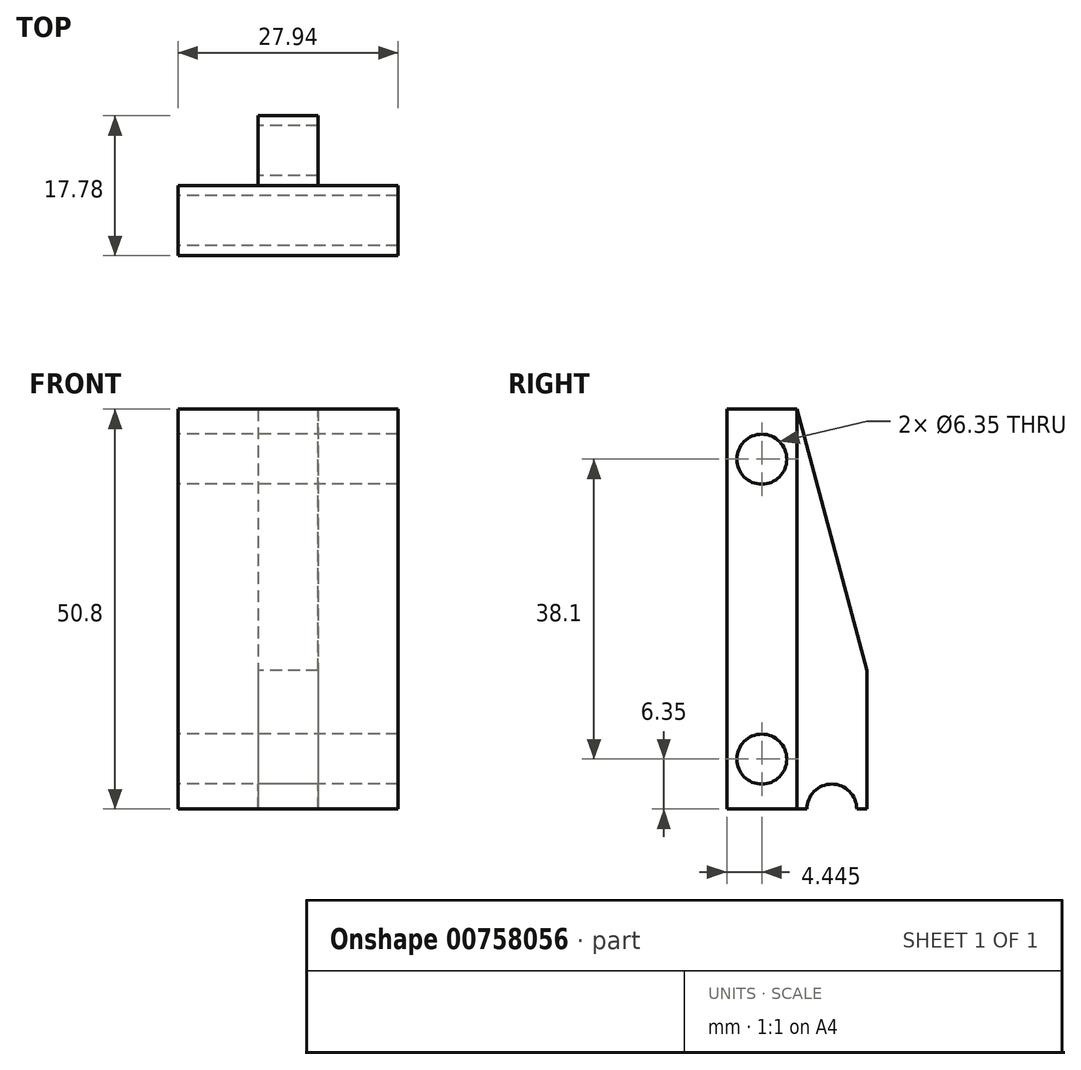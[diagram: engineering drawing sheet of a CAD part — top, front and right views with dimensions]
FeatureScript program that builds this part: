
annotation { "Feature Type Name" : "Feature", "Feature Type Description" : "" }
export const myFeature = defineFeature(function(context is Context, id is Id, definition is map)
    precondition{}
    {
        {
            var Q0;
            Q0=qCreatedBy(makeId("Top.planeOp"),FACE);
            var sketch = newSketch(context, id + "F0", { "sketchPlane" : qUnion([Q0])});
            skLineSegment(sketch, "E0.bottom", {"start": v(0, 0) * mm, "end": v(27.94, 0) * mm});
            skLineSegment(sketch, "E0.top", {"start": v(0, 17.78) * mm, "end": v(27.94, 17.78) * mm});
            skLineSegment(sketch, "E0.left", {"start": v(0, 0) * mm, "end": v(0, 17.78) * mm});
            skLineSegment(sketch, "E0.right", {"start": v(27.94, 0) * mm, "end": v(27.94, 17.78) * mm});
            skLineSegment(sketch, "E1.bottom", {"start": v(0, 8.89) * mm, "end": v(10.16, 8.89) * mm});
            skLineSegment(sketch, "E1.top", {"start": v(0, 17.78) * mm, "end": v(10.16, 17.78) * mm});
            skLineSegment(sketch, "E1.left", {"start": v(0, 8.89) * mm, "end": v(0, 17.78) * mm});
            skLineSegment(sketch, "E1.right", {"start": v(10.16, 8.89) * mm, "end": v(10.16, 17.78) * mm});
            skLineSegment(sketch, "E2.bottom", {"start": v(17.78, 17.78) * mm, "end": v(27.94, 17.78) * mm});
            skLineSegment(sketch, "E2.top", {"start": v(17.78, 8.89) * mm, "end": v(27.94, 8.89) * mm});
            skLineSegment(sketch, "E2.left", {"start": v(17.78, 17.78) * mm, "end": v(17.78, 8.89) * mm});
            skLineSegment(sketch, "E2.right", {"start": v(27.94, 17.78) * mm, "end": v(27.94, 8.89) * mm});
            skSolve(sketch);
        }
        {
            var Q0;
            {var subQ1=sQuery(id+"F0.wireOp",EDGE,"E0.bottom");Q0=makeQuery(id+"F0.imprint","IMPRINT",FACE,{"disambiguationData":[TD([[makeQuery(id+"F0.imprint","IMPRINT",EDGE,{"derivedFrom":subQ1}),1.0]])]});}
            extrude(context, id + "F1", {"entities" : qUnion([Q0]), "depth" : 50.8 * mm, "offsetDistance" : 25.4 * mm});
        }
        {
            var Q0;
            Q0=makeQuery(id+"F1.opExtrude","SWEPT_FACE",FACE,{"disambiguationData":[OSD([sQuery(id+"F0.wireOp",EDGE,"E1.right")])]});
            var sketch = newSketch(context, id + "F2", { "sketchPlane" : qUnion([Q0])});
            skLineSegment(sketch, "E3", {"start": v(-8.89, 50.8) * mm, "end": v(-17.78, 17.62) * mm});
            skCircle(sketch, "E4", {"center": v(-13.33, 0) * mm, "radius": 3.18 * mm});
            skSolve(sketch);
        }
        {
            var Q0;
            {var subQ0=sQuery(id+"F2.wireOp",EDGE,"E3");Q0=makeQuery(id+"F2.imprint","IMPRINT",FACE,{"disambiguationData":[TD([[makeQuery(id+"F2.imprint","IMPRINT",EDGE,{"derivedFrom":subQ0}),-1.0]])]});}
            var Q1;
            {var subQ0=sQuery(id+"F2.wireOp",EDGE,"E4");var subQ1=makeQuery(id+"F1.opExtrude","CAP_EDGE",EDGE,{"disambiguationData":[OSD([sQuery(id+"F0.wireOp",EDGE,"E1.right")])],"isStart":true});var subQ2=makeQuery(id+"F2.imprint","INTERSECT",VERTEX,{"disambiguationData":[OD(0.0)],"derivedFrom":[subQ1,subQ0]});Q1=makeQuery(id+"F2.imprint","IMPRINT",FACE,{"disambiguationData":[TD([[makeQuery(id+"F2.imprint","IMPRINT",EDGE,{"disambiguationData":[TD([[subQ2,-1.0]])],"derivedFrom":subQ0}),1.0]])]});}
            extrude(context, id + "F3", {"entities" : qUnion([Q0, Q1]), "operationType" : NewBodyOperationType.REMOVE, "oppositeDirection" : true, "depth" : 25.4 * mm, "offsetDistance" : 25.4 * mm});
        }
        {
            var Q0;
            Q0=makeQuery(id+"F1.opExtrude","SWEPT_FACE",FACE,{"disambiguationData":[OSD([sQuery(id+"F0.wireOp",EDGE,"E0.left")])]});
            var sketch = newSketch(context, id + "F4", { "sketchPlane" : qUnion([Q0])});
            skCircle(sketch, "E5", {"center": v(-4.44, 44.45) * mm, "radius": 3.18 * mm});
            skCircle(sketch, "E6", {"center": v(-4.44, 6.35) * mm, "radius": 3.18 * mm});
            skLineSegment(sketch, "E7", {"start": v(-4.44, 50.8) * mm, "end": v(-4.44, 0) * mm, "construction": true});
            skSolve(sketch);
        }
        {
            var Q0;
            Q0=makeQuery(id+"F4.imprint","IMPRINT",FACE,{"disambiguationData":[TD([[makeQuery(id+"F4.imprint","IMPRINT",EDGE,{"derivedFrom":sQuery(id+"F4.wireOp",EDGE,"E5")}),1.0]])]});
            var Q1;
            Q1=makeQuery(id+"F4.imprint","IMPRINT",FACE,{"disambiguationData":[TD([[makeQuery(id+"F4.imprint","IMPRINT",EDGE,{"derivedFrom":sQuery(id+"F4.wireOp",EDGE,"E6")}),1.0]])]});
            extrude(context, id + "F5", {"entities" : qUnion([Q0, Q1]), "operationType" : NewBodyOperationType.REMOVE, "oppositeDirection" : true, "depth" : 38.1 * mm, "offsetDistance" : 25.4 * mm});
        }
    });
